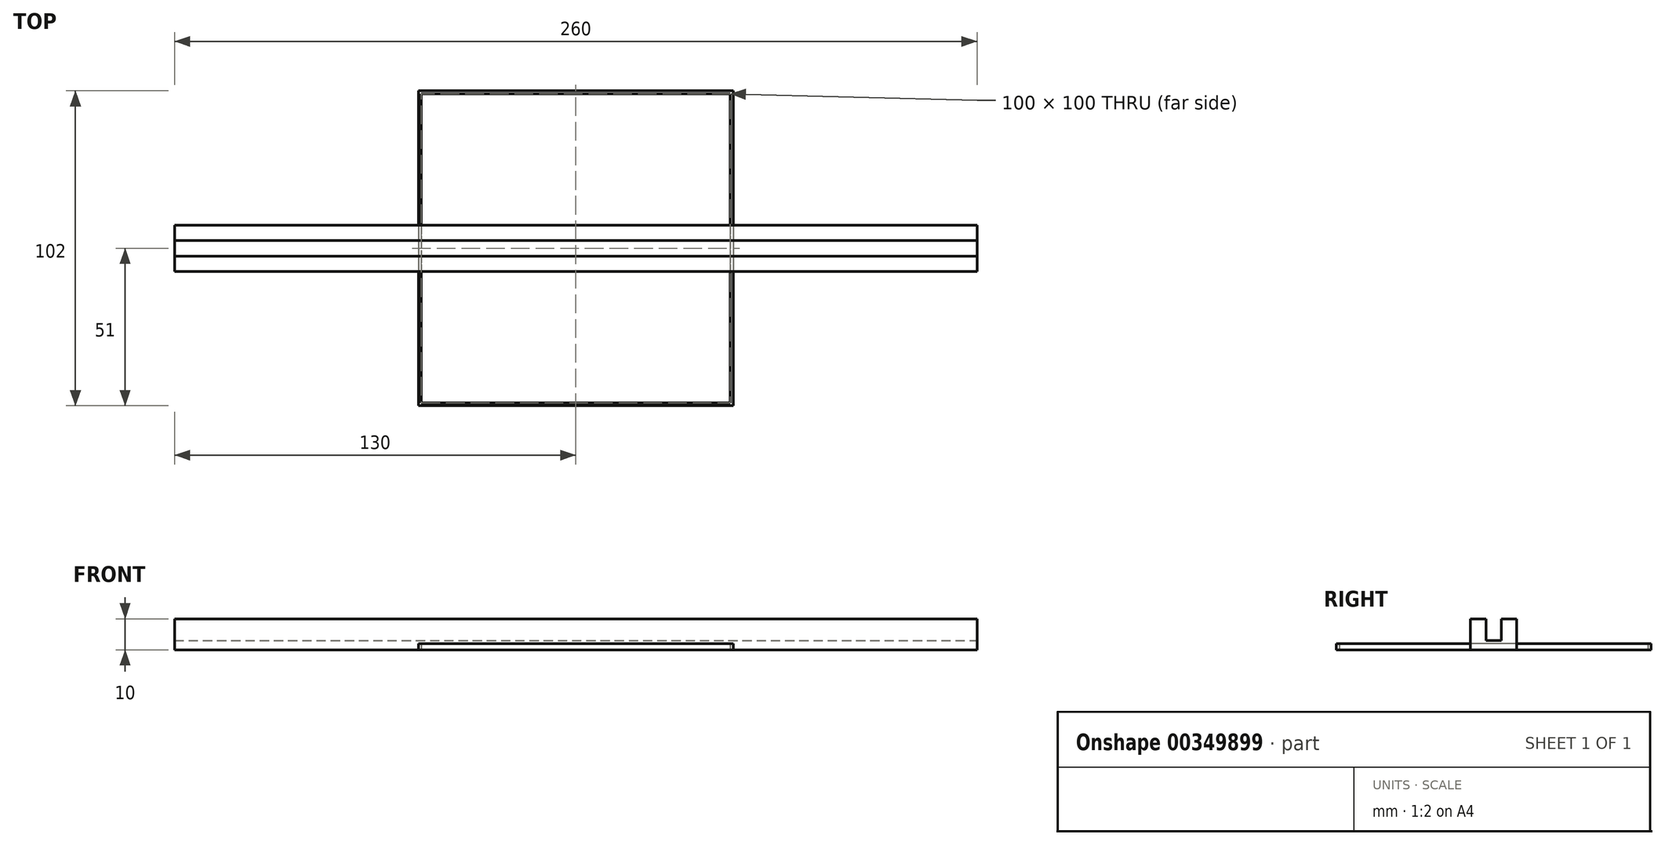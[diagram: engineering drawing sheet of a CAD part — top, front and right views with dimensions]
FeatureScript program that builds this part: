
annotation { "Feature Type Name" : "Feature", "Feature Type Description" : "" }
export const myFeature = defineFeature(function(context is Context, id is Id, definition is map)
    precondition{}
    {
        {
            var Q0;
            Q0=qCreatedBy(makeId("Top.planeOp"),FACE);
            var sketch = newSketch(context, id + "F0", { "sketchPlane" : qUnion([Q0])});
            skLineSegment(sketch, "E0.bottom", {"start": v(50, 50) * mm, "end": v(-50, 50) * mm});
            skLineSegment(sketch, "E0.top", {"start": v(50, -50) * mm, "end": v(-50, -50) * mm});
            skLineSegment(sketch, "E0.left", {"start": v(50, 50) * mm, "end": v(50, -50) * mm});
            skLineSegment(sketch, "E0.right", {"start": v(-50, 50) * mm, "end": v(-50, -50) * mm});
            skPoint(sketch, "E0.middle", {"position": v(0, 0) * mm});
            skLineSegment(sketch, "E1.0", {"start": v(-51, 51) * mm, "end": v(-51, -51) * mm});
            skLineSegment(sketch, "E1.1", {"start": v(51, 51) * mm, "end": v(-51, 51) * mm});
            skLineSegment(sketch, "E1.2", {"start": v(51, 51) * mm, "end": v(51, -51) * mm});
            skLineSegment(sketch, "E1.3", {"start": v(51, -51) * mm, "end": v(-51, -51) * mm});
            skSolve(sketch);
        }
        {
            var Q0;
            Q0=makeQuery(id+"F0.imprint","IMPRINT",FACE,{"disambiguationData":[TD([[makeQuery(id+"F0.imprint","IMPRINT",EDGE,{"derivedFrom":sQuery(id+"F0.wireOp",EDGE,"E0.bottom")}),-1.0]])]});
            extrude(context, id + "F1", {"entities" : qUnion([Q0]), "depth" : 2 * mm});
        }
        {
            var Q0;
            Q0=qCreatedBy(makeId("Top.planeOp"),FACE);
            var sketch = newSketch(context, id + "F2", { "sketchPlane" : qUnion([Q0])});
            skLineSegment(sketch, "E2.bottom", {"start": v(130, -7.5) * mm, "end": v(-130, -7.5) * mm});
            skLineSegment(sketch, "E2.top", {"start": v(130, 7.5) * mm, "end": v(-130, 7.5) * mm});
            skLineSegment(sketch, "E2.left", {"start": v(130, -7.5) * mm, "end": v(130, 7.5) * mm});
            skLineSegment(sketch, "E2.right", {"start": v(-130, -7.5) * mm, "end": v(-130, 7.5) * mm});
            skPoint(sketch, "E2.middle", {"position": v(0, 0) * mm});
            skSolve(sketch);
        }
        {
            var Q0;
            Q0 = qSketchRegion(id + "F2", true);
            extrude(context, id + "F3", {"entities" : qUnion([Q0]), "depth" : 10 * mm});
        }
        {
            var Q0;
            Q0=makeQuery(id+"F3.opExtrude","CAP_FACE",FACE,{"disambiguationData":[OSD([sQuery(id+"F2.wireOp",EDGE,"E2.bottom"),sQuery(id+"F2.wireOp",EDGE,"E2.top"),sQuery(id+"F2.wireOp",EDGE,"E2.left"),sQuery(id+"F2.wireOp",EDGE,"E2.right")])],"isStart":false});
            var sketch = newSketch(context, id + "F4", { "sketchPlane" : qUnion([Q0])});
            skLineSegment(sketch, "E3", {"start": v(-130, 0) * mm, "end": v(-130, 2.5) * mm, "construction": true});
            skLineSegment(sketch, "E4.bottom", {"start": v(-130, 2.5) * mm, "end": v(130, 2.5) * mm});
            skLineSegment(sketch, "E4.top", {"start": v(-130, -2.5) * mm, "end": v(130, -2.5) * mm});
            skLineSegment(sketch, "E4.left", {"start": v(-130, 2.5) * mm, "end": v(-130, -2.5) * mm});
            skLineSegment(sketch, "E4.right", {"start": v(130, 2.5) * mm, "end": v(130, -2.5) * mm});
            skSolve(sketch);
        }
        {
            var Q0;
            Q0 = qSketchRegion(id + "F4", true);
            extrude(context, id + "F5", {"entities" : qUnion([Q0]), "operationType" : NewBodyOperationType.REMOVE, "oppositeDirection" : true, "depth" : 7 * mm});
        }
    });
